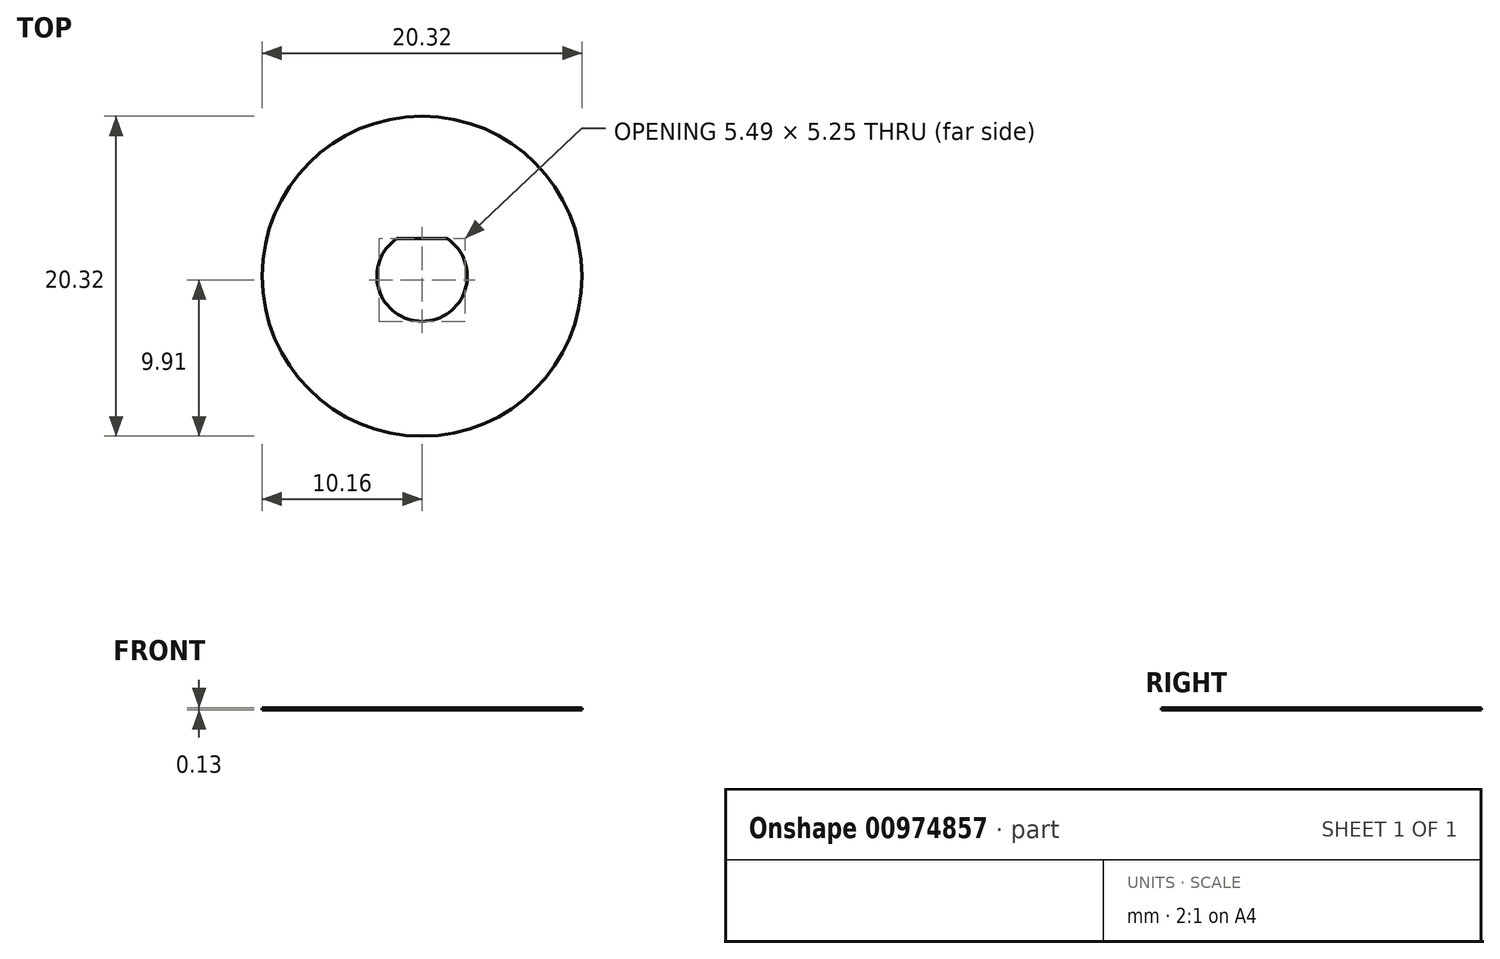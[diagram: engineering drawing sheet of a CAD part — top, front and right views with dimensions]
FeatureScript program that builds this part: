
annotation { "Feature Type Name" : "Feature", "Feature Type Description" : "" }
export const myFeature = defineFeature(function(context is Context, id is Id, definition is map)
    precondition{}
    {
        {
            assignVariable(context, id + "F0", {"name" : "thin_mdf_thickness", "anyValue" : 0.12});
        }
        {
            var Q0;
            Q0=qCreatedBy(makeId("Top.planeOp"),FACE);
            var sketch = newSketch(context, id + "F1", { "sketchPlane" : qUnion([Q0])});
            skArc(sketch, "E0", {"start": v(-1.66, 2.5) * mm, "mid": v(0, -3) * mm, "end": v(1.66, 2.5) * mm, "construction": true});
            skLineSegment(sketch, "E1", {"start": v(0, 0) * mm, "end": v(0, -3) * mm, "construction": true});
            skLineSegment(sketch, "E2", {"start": v(0, -3) * mm, "end": v(0, 2.5) * mm, "construction": true});
            skLineSegment(sketch, "E3", {"start": v(0, 2.5) * mm, "end": v(1.66, 2.5) * mm, "construction": true});
            skLineSegment(sketch, "E4", {"start": v(0, 2.5) * mm, "end": v(-1.66, 2.5) * mm, "construction": true});
            skArc(sketch, "E5.0", {"start": v(-1.62, 2.37) * mm, "mid": v(0, -2.87) * mm, "end": v(1.62, 2.37) * mm});
            skLineSegment(sketch, "E5.1", {"start": v(0, 2.37) * mm, "end": v(-1.62, 2.37) * mm});
            skLineSegment(sketch, "E5.2", {"start": v(0, 2.37) * mm, "end": v(1.62, 2.37) * mm});
            skCircle(sketch, "E6", {"center": v(0, 0) * mm, "radius": 10.16 * mm});
            skSolve(sketch);
        }
        {
            var Q0;
            Q0=makeQuery(id+"F1.imprint","IMPRINT",FACE,{"disambiguationData":[TD([[makeQuery(id+"F1.imprint","IMPRINT",EDGE,{"derivedFrom":sQuery(id+"F1.wireOp",EDGE,"E5.0")}),-1.0]])]});
            extrude(context, id + "F2", {"entities" : qUnion([Q0]), "depth" : (getVariable(context, 'thin_mdf_thickness')) * mm, "offsetDistance" : 25.4 * mm});
        }
    });
